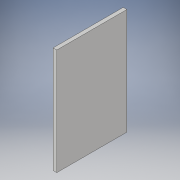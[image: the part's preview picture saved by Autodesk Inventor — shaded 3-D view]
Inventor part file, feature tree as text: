
AUTODESK INVENTOR PART (.ipt)
format: ipt  version: 2017 (Build 210142000, 142)  size: 89,088 bytes
history: native  units: in
note: dims shown in document units (in); Inventor stores cm internally (conversion verified against a paired STEP export)
features: extrude x1, sketch x1
ambient origin geometry x8: Origin, YZ Plane, XZ Plane, XY Plane, X Axis, Y Axis, Z Axis, Center Point
bodies: Solid1 (feature_tree)
feature tree (2):
  extrude  "Extrusion1"  Depth=9.5in
  sketch  "Sketch1"  dims[d0=14.366in d1=9.5in d2=0.5in d3=0.0in]
